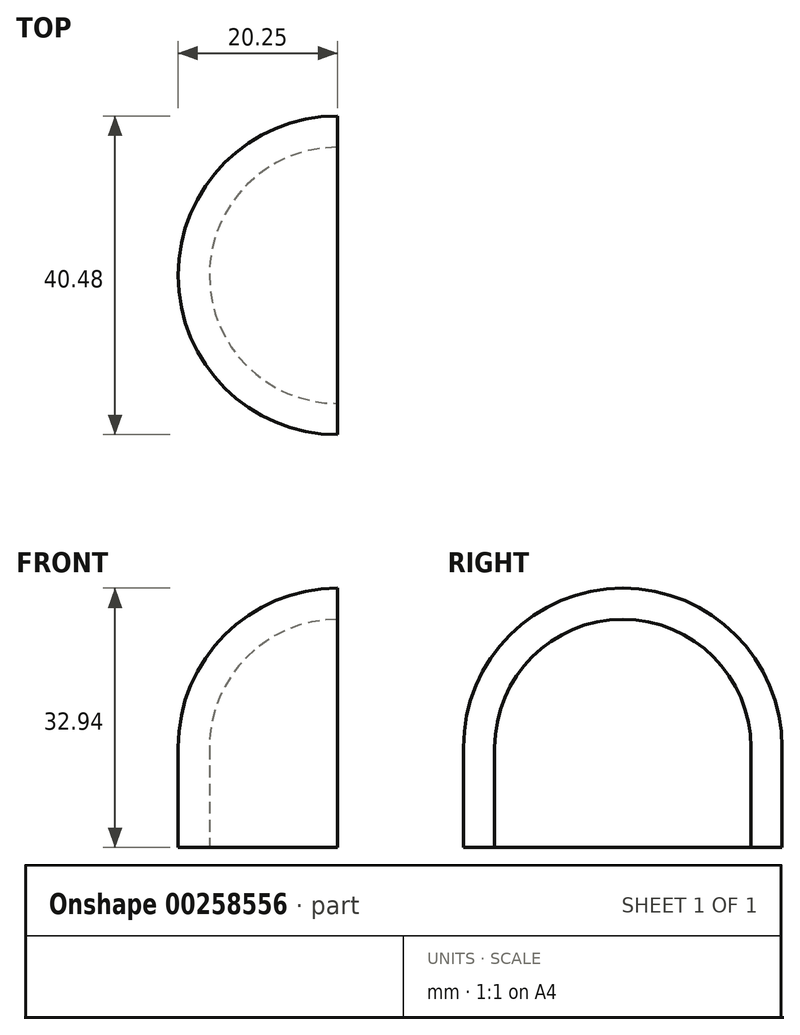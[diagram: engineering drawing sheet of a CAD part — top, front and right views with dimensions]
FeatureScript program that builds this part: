
annotation { "Feature Type Name" : "Feature", "Feature Type Description" : "" }
export const myFeature = defineFeature(function(context is Context, id is Id, definition is map)
    precondition{}
    {
        {
            var Q0;
            Q0=qCreatedBy(makeId("Top.planeOp"),FACE);
            var sketch = newSketch(context, id + "F0", { "sketchPlane" : qUnion([Q0])});
            skCircle(sketch, "E0", {"center": v(28.62, 0) * mm, "radius": 16.27 * mm});
            skCircle(sketch, "E1", {"center": v(28.62, 0) * mm, "radius": 20.24 * mm});
            skCircle(sketch, "E2", {"center": v(0, 28.62) * mm, "radius": 16.27 * mm});
            skCircle(sketch, "E3", {"center": v(0, 28.62) * mm, "radius": 20.24 * mm});
            skCircle(sketch, "E4", {"center": v(-28.62, 0) * mm, "radius": 16.27 * mm});
            skCircle(sketch, "E5", {"center": v(-28.62, 0) * mm, "radius": 20.24 * mm});
            skCircle(sketch, "E6", {"center": v(0, -28.62) * mm, "radius": 20.24 * mm});
            skCircle(sketch, "E7", {"center": v(0, -28.62) * mm, "radius": 16.27 * mm});
            skLineSegment(sketch, "E8", {"start": v(0, 0) * mm, "end": v(-28.62, 0) * mm, "construction": true});
            skLineSegment(sketch, "E9", {"start": v(0, 0) * mm, "end": v(28.62, 0) * mm, "construction": true});
            skLineSegment(sketch, "E10", {"start": v(0, 0) * mm, "end": v(0, 28.62) * mm, "construction": true});
            skLineSegment(sketch, "E11", {"start": v(0, 0) * mm, "end": v(0, -28.62) * mm, "construction": true});
            skLineSegment(sketch, "E12", {"start": v(0, 0) * mm, "end": v(-27.5, 0) * mm});
            skLineSegment(sketch, "E13", {"start": v(-28.62, 20.24) * mm, "end": v(-28.62, -20.24) * mm});
            skSolve(sketch);
        }
        {
            var Q0;
            {var subQ0=sQuery(id+"F0.wireOp",EDGE,"E13");var subQ1=sQuery(id+"F0.wireOp",EDGE,"E4");var subQ2=makeQuery(id+"F0.imprint","INTERSECT",VERTEX,{"disambiguationData":[OD(0.0)],"derivedFrom":[subQ1,subQ0]});Q0=makeQuery(id+"F0.imprint","IMPRINT",FACE,{"disambiguationData":[TD([[makeQuery(id+"F0.imprint","IMPRINT",EDGE,{"disambiguationData":[TD([[subQ2,-1.0]])],"derivedFrom":subQ1}),-1.0]])]});}
            extrude(context, id + "F1", {"entities" : qUnion([Q0]), "depth" : 12.7 * mm});
        }
        {
            var Q0;
            Q0=qCreatedBy(makeId("Front.planeOp"),FACE);
            var sketch = newSketch(context, id + "F2", { "sketchPlane" : qUnion([Q0])});
            skArc(sketch, "E14", {"start": v(-28.62, 32.94) * mm, "mid": v(-42.94, 27.01) * mm, "end": v(-48.87, 12.7) * mm});
            skLineSegment(sketch, "E15", {"start": v(-48.87, 12.7) * mm, "end": v(-48.87, 0) * mm, "construction": true});
            skLineSegment(sketch, "E16", {"start": v(-28.62, 32.94) * mm, "end": v(-28.62, 12.7) * mm, "construction": true});
            skLineSegment(sketch, "E17", {"start": v(-28.62, 32.94) * mm, "end": v(-21.63, 32.94) * mm, "construction": true});
            skArc(sketch, "E18", {"start": v(-28.62, 28.97) * mm, "mid": v(-40.13, 24.2) * mm, "end": v(-44.9, 12.7) * mm});
            skLineSegment(sketch, "E19", {"start": v(-44.9, 12.7) * mm, "end": v(-48.87, 12.7) * mm});
            skLineSegment(sketch, "E20", {"start": v(-28.62, 32.94) * mm, "end": v(-28.62, 28.97) * mm});
            skSolve(sketch);
        }
        {
            var Q0;
            Q0 = qSketchRegion(id + "F2", true);
            var Q1;
            Q1=sQuery(id+"F2.wireOp",EDGE,"E16");
            revolve(context, id + "F3", {"operationType" : NewBodyOperationType.ADD, "entities" : qUnion([Q0]), "axis" : qUnion([Q1]), "revolveType" : RevolveType.TWO_DIRECTIONS, "angle" : 90 * degree, "angleBack" : 270 * degree});
        }
    });
